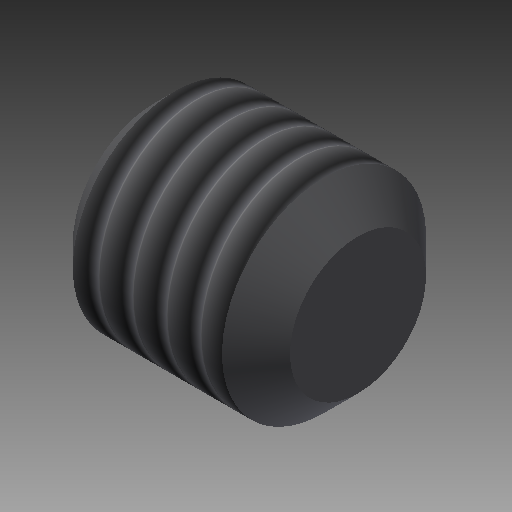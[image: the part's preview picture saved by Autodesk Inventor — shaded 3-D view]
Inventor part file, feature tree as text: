
AUTODESK INVENTOR PART (.ipt)
format: ipt  version: 2017 (Build 210142000, 142)  size: 182,272 bytes
history: native  units: mm
features: other x7, sketch x3, revolve x2, thread x1, extrude x1
ambient origin geometry x8: Origin, YZ Plane, XZ Plane, XY Plane, X Axis, Y Axis, Z Axis, Center Point
bodies: Solid1 (feature_tree)
feature tree (14):
  revolve  "Revolution1"  [1 undecoded]
  thread  "Thread1"  [1 undecoded]
  extrude  "Extrusion1"  TaperAngle=0.0deg  [1 undecoded]
  revolve  "Revolution2"  [1 undecoded]
  other  "CP_XY"
  other  "CP_YZ"
  other  "CP_ZX"
  other  "CP_X"
  other  "CP_Y"
  other  "CP_Z"
  other  "CP_Center"
  sketch  "Sketch_1"  dims[d0=360.0deg d1=2.1935mm d2=0.0mm d3=1.2mm d4=0.0mm]
  sketch  "Sketch_2"  dims[d5=360.0deg d6=0.0mm]
  sketch  "Sketch_3"
note: 4 required parameter values undecoded (feature->parameter linkage not recoverable at this tier; creation-order binding heuristic only, values carry confidence <= 0.55)